FCSTD DOCUMENT  (FreeCAD 0.21R33771 (Git))
Label: jrobot-electronics-print-orientations
License: All rights reserved
LicenseURL: http://en.wikipedia.org/wiki/All_rights_reserved
objects: App::DocumentObjectGroup×3, PartDesign::CoordinateSystem×3, App::Link×2, App::FeaturePython×1, App::Part×1
note: 3 computed .brp shape members not serialized (recipe doc carries the construction recipe); baked Part::Feature solids carry a one-line shape summary decoded from their .brp
EXTERNAL_REF file=jrobot-electronics-parts.FCStd obj=LCS_Origin006
EXTERNAL_REF file=jrobot-electronics-parts.FCStd obj=P_ElectronicsBox
EXTERNAL_REF file=jrobot-electronics-parts.FCStd obj=LCS_Origin007
EXTERNAL_REF file=jrobot-electronics-parts.FCStd obj=P_ElectronicsBox_Cover

FEATURE [App::DocumentObjectGroup] Parts
FEATURE [PartDesign::CoordinateSystem] LCS_Origin
  AttacherType = Attacher::AttachEngine3D
  MapMode = 2
  Support = -> [X_Axis]
FEATURE [App::DocumentObjectGroup] Constraints
FEATURE [App::FeaturePython] Variables  # WARN: FeaturePython — macro-defined, semantics opaque (R4)
  Type = App::PropertyContainer
FEATURE [App::DocumentObjectGroup] Configurations
FEATURE [PartDesign::CoordinateSystem] LCS_ElectronicsBox_Base
  AttacherType = Attacher::AttachEngine3D
FEATURE [PartDesign::CoordinateSystem] LCS_ElectronicsBox_Cover
  AttacherType = Attacher::AttachEngine3D
  Placement = pos=(200,0,0) rot=(0,0,1;0rad)
FEATURE [App::Link] P_ElectronicsBox_Base
  AttachedBy = #LCS_Origin006
  AttachedTo = Parent Assembly#LCS_ElectronicsBox_Base
  LinkedObject = -> <external jrobot-electronics-parts.FCStd>#P_ElectronicsBox
  SolverId = Asm4EE
  expr: Placement = LCS_ElectronicsBox_Base.Placement * AttachmentOffset * jrobot_electronics_parts#LCS_Origin006.Placement ^ -1
FEATURE [App::Link] P_ElectronicsBox_Cover
  AttachedBy = #LCS_Origin007
  AttachedTo = Parent Assembly#LCS_ElectronicsBox_Cover
  AttachmentOffset = pos=(0,0,0) rot=(1,0,0;3.14159rad)
  LinkPlacement = pos=(200,0,0) rot=(1,0,0;3.14159rad)
  LinkedObject = -> <external jrobot-electronics-parts.FCStd>#P_ElectronicsBox_Cover
  Placement = pos=(200,0,0) rot=(1,0,0;3.14159rad)
  SolverId = Asm4EE
  expr: Placement = LCS_ElectronicsBox_Cover.Placement * AttachmentOffset * jrobot_electronics_parts#LCS_Origin007.Placement ^ -1
FEATURE [App::Part] Assembly
  AssemblyType = Part::Link
  Group = -> [LCS_Origin,Constraints,Variables,Configurations,LCS_ElectronicsBox_Base,LCS_ElectronicsBox_Cover,P_ElectronicsBox_Base,P_ElectronicsBox_Cover]
  Origin = -> Origin
  Type = Assembly

RESOLVED EXTERNAL PARTS (link-assembly join: the EXTERNAL_REF files above that resolve inside this repo's crawl, each included once):
---- part jrobot-electronics-parts.FCStd = doc fcstd_2911611a7a01 ----
FCSTD DOCUMENT  (FreeCAD 0.21R33771 (Git))
Label: jrobot-electronics-parts
License: All rights reserved
LicenseURL: http://en.wikipedia.org/wiki/All_rights_reserved
objects: PartDesign::CoordinateSystem×24, Sketcher::SketchObject×16, PartDesign::Pocket×7, PartDesign::Pad×5, PartDesign::Mirrored×3, App::DocumentObjectGroup×3, PartDesign::MultiTransform×2, PartDesign::Body×2, App::Part×2, PartDesign::LinearPattern×2, PartDesign::AdditiveLoft×1
note: 75 computed .brp shape members not serialized (recipe doc carries the construction recipe); baked Part::Feature solids carry a one-line shape summary decoded from their .brp

FEATURE [PartDesign::CoordinateSystem] LCS_ElectronicsBox_Lid
  AttacherType = Attacher::AttachEngine3D
  Placement = pos=(0,0,56) rot=(0,0,1;0rad)
FEATURE [PartDesign::CoordinateSystem] LCS_Origin006  label="LCS_ElectronicsBox_Origin"
  AttacherType = Attacher::AttachEngine3D
  MapMode = 2
  Support = -> [X_Axis026]
FEATURE [Sketcher::SketchObject] Sketch034  label="S_ElectronicsBox_HoleLocations"
  FullyConstrained = true
  Support = -> [XY_Plane027]
  sketch-geometry (27):
    g0: LineSegment StartX=-85 StartY=73 StartZ=0 EndX=-85 EndY=-73 EndZ=0
    g1: LineSegment StartX=-85 StartY=-73 StartZ=0 EndX=85 EndY=-73 EndZ=0
    g2: LineSegment StartX=85 StartY=-73 StartZ=0 EndX=85 EndY=73 EndZ=0
    g3: LineSegment StartX=85 StartY=73 StartZ=0 EndX=-85 EndY=73 EndZ=0
    g4: GeomPoint X=0 Y=0 Z=0
    g5: LineSegment StartX=5 StartY=63 StartZ=0 EndX=74 EndY=63 EndZ=0
    g6: LineSegment StartX=74 StartY=63 StartZ=0 EndX=74 EndY=10 EndZ=0
    g7: LineSegment StartX=74 StartY=10 StartZ=0 EndX=5 EndY=10 EndZ=0
    g8: LineSegment StartX=5 StartY=10 StartZ=0 EndX=5 EndY=63 EndZ=0
    g9: LineSegment StartX=5 StartY=-10 StartZ=0 EndX=74 EndY=-10 EndZ=0
    g10: LineSegment StartX=74 StartY=-10 StartZ=0 EndX=74 EndY=-63 EndZ=0
    g11: LineSegment StartX=74 StartY=-63 StartZ=0 EndX=5 EndY=-63 EndZ=0
    g12: LineSegment StartX=5 StartY=-63 StartZ=0 EndX=5 EndY=-10 EndZ=0
    g13: LineSegment StartX=-60 StartY=54 StartZ=0 EndX=-5 EndY=54 EndZ=0
    g14: LineSegment StartX=-5 StartY=54 StartZ=0 EndX=-5 EndY=-54 EndZ=0
    g15: LineSegment StartX=-5 StartY=-54 StartZ=0 EndX=-60 EndY=-54 EndZ=0
    g16: LineSegment StartX=-60 StartY=-54 StartZ=0 EndX=-60 EndY=54 EndZ=0
    g17: GeomPoint X=19.25 Y=60 Z=0
    g18: GeomPoint X=19.25 Y=13 Z=0
    g19: GeomPoint X=19.25 Y=-60 Z=0
    g20: GeomPoint X=19.25 Y=-13 Z=0
    g21: GeomPoint X=59 Y=37 Z=0
    g22: GeomPoint X=59 Y=-36 Z=0
    g23: GeomPoint X=-56 Y=36.5 Z=0
    g24: GeomPoint X=-8 Y=41.5 Z=0
    g25: GeomPoint X=-56 Y=-39 Z=0
    g26: GeomPoint X=-8 Y=-40.5 Z=0
  constraints (70):
    c: Coincident(g0,g1)
    c: Coincident(g1,g2)
    c: Coincident(g2,g3)
    c: Coincident(g3,g0)
    c: Horizontal(g1)
    c: Horizontal(g3)
    c: Vertical(g0)
    c: Vertical(g2)
    c: Symmetric(g1,g0,g4)
    c: Coincident(g4,g-1)
    c: Coincident(g5,g6)
    c: Coincident(g6,g7)
    c: Coincident(g7,g8)
    c: Coincident(g8,g5)
    c: Horizontal(g5)
    c: Horizontal(g7)
    c: Vertical(g6)
    c: Vertical(g8)
    c: DistanceX(g5,g5) = 69
    c: DistanceY(g6,g6) = 53
    c: Coincident(g9,g10)
    c: Coincident(g10,g11)
    c: Coincident(g11,g12)
    c: Coincident(g12,g9)
    c: Horizontal(g9)
    c: Horizontal(g11)
    c: Vertical(g10)
    c: Vertical(g12)
    c: Equal(g7,g9)
    c: Equal(g6,g10)
    c: Vertical(g7,g9)
    c: DistanceY(g9,g7) = 20
    c: DistanceY(g4,g7) = 10
    c: Coincident(g13,g14)
    c: Coincident(g14,g15)
    c: Coincident(g15,g16)
    c: Coincident(g16,g13)
    c: Horizontal(g13)
    c: Horizontal(g15)
    c: Vertical(g16)
    c: DistanceX(g13,g13) = 55
    c: DistanceY(g14,g14) = 108
    c: DistanceX(g13,g4) = 5
    c: DistanceX(g4,g5) = 5
    c: Symmetric(g13,g14,g-1)
    c: DistanceX(g0,g13) = 25
    c: DistanceY(g17,g5) = 3
    c: DistanceY(g7,g18) = 3
    c: DistanceX(g7,g18) = 14.25
    c: Vertical(g18,g17)
    c: DistanceX(g11,g19) = 14.25
    c: DistanceY(g11,g19) = 3
    c: DistanceY(g20,g9) = 3
    c: Vertical(g20,g19)
    c: Vertical(g21,g22)
    c: DistanceY(g21,g5) = 26
    c: DistanceY(g22,g9) = 26
    c: DistanceY(g2,g2) = 146
    c: DistanceY(g25,g23) = 75.5
    c: DistanceX(g15,g25) = 4
    c: DistanceY(g15,g25) = 15
    c: Vertical(g23,g25)
    c: DistanceY(g14,g26) = 13.5
    c: DistanceX(g26,g14) = 3
    c: Vertical(g24,g26)
    c: DistanceY(g26,g24) = 82
    c: DistanceX(g22,g10) = 15
    c: DistanceY(g18,g17) = 47  'HoleYSeparation1'
    c: DistanceY(g18,g21) = 24  'HoleYSeparation0'
    c: DistanceX(g18,g21) = 39.75  'HoleXSeparation'
FEATURE [Sketcher::SketchObject] Sketch033  label="S_ElectronicsBox_Base"
  ExternalGeometry = -> [Sketch034]
  FullyConstrained = true
  MapMode = 5
  Support = -> [XY_Plane027]
  sketch-geometry (24):
    g0: LineSegment StartX=-85 StartY=73 StartZ=0 EndX=-85 EndY=63 EndZ=0
    g1: LineSegment StartX=-85 StartY=-73 StartZ=0 EndX=85 EndY=-73 EndZ=0
    g2: LineSegment StartX=85 StartY=73 StartZ=0 EndX=-85 EndY=73 EndZ=0
    g3: LineSegment StartX=-85 StartY=63 StartZ=0 EndX=-95 EndY=63 EndZ=0
    g4: LineSegment StartX=-95 StartY=63 StartZ=0 EndX=-95 EndY=53 EndZ=0
    g5: LineSegment StartX=-95 StartY=53 StartZ=0 EndX=-85 EndY=53 EndZ=0
    g6: LineSegment StartX=-85 StartY=-53 StartZ=0 EndX=-95 EndY=-53 EndZ=0
    g7: LineSegment StartX=-95 StartY=-53 StartZ=0 EndX=-95 EndY=-63 EndZ=0
    g8: LineSegment StartX=-95 StartY=-63 StartZ=0 EndX=-85 EndY=-63 EndZ=0
    g9: LineSegment StartX=85 StartY=63 StartZ=0 EndX=95 EndY=63 EndZ=0
    g10: LineSegment StartX=95 StartY=63 StartZ=0 EndX=95 EndY=53 EndZ=0
    g11: LineSegment StartX=95 StartY=53 StartZ=0 EndX=85 EndY=53 EndZ=0
    g12: LineSegment StartX=85 StartY=-53 StartZ=0 EndX=95 EndY=-53 EndZ=0
    g13: LineSegment StartX=95 StartY=-53 StartZ=0 EndX=95 EndY=-63 EndZ=0
    g14: LineSegment StartX=95 StartY=-63 StartZ=0 EndX=85 EndY=-63 EndZ=0
    g15: LineSegment StartX=-85 StartY=-63 StartZ=0 EndX=-85 EndY=-73 EndZ=0
    g16: LineSegment StartX=-85 StartY=53 StartZ=0 EndX=-85 EndY=-53 EndZ=0
    g17: LineSegment StartX=85 StartY=-73 StartZ=0 EndX=85 EndY=-63 EndZ=0
    g18: LineSegment StartX=85 StartY=-53 StartZ=0 EndX=85 EndY=53 EndZ=0
    g19: LineSegment StartX=85 StartY=63 StartZ=0 EndX=85 EndY=73 EndZ=0
    g20: Circle CenterX=-90 CenterY=-58 CenterZ=0 NormalX=0 NormalY=0 NormalZ=1 AngleXU=0 Radius=2.5
    g21: Circle CenterX=-90 CenterY=58 CenterZ=0 NormalX=0 NormalY=0 NormalZ=1 AngleXU=0 Radius=2.5
    g22: Circle CenterX=90 CenterY=58 CenterZ=0 NormalX=0 NormalY=0 NormalZ=1 AngleXU=0 Radius=2.5
    g23: Circle CenterX=90 CenterY=-58 CenterZ=0 NormalX=0 NormalY=0 NormalZ=1 AngleXU=0 Radius=2.5
  constraints (70):
    c: Coincident(g2,g0)
    c: Horizontal(g1)
    c: Horizontal(g2)
    c: Vertical(g0)
    c: Symmetric(g1,g0,g-1)
    c: Coincident(g0,g-3)
    c: Coincident(g3,g4)
    c: Coincident(g4,g5)
    c: Horizontal(g3)
    c: Horizontal(g5)
    c: Vertical(g4)
    c: Coincident(g6,g7)
    c: Coincident(g7,g8)
    c: Horizontal(g6)
    c: Horizontal(g8)
    c: Vertical(g7)
    c: PointOnObject(g6,g0)
    c: Coincident(g9,g10)
    c: Coincident(g10,g11)
    c: Horizontal(g9)
    c: Horizontal(g11)
    c: Vertical(g10)
    c: Coincident(g12,g13)
    c: Coincident(g13,g14)
    c: Horizontal(g12)
    c: Horizontal(g14)
    c: Vertical(g13)
    c: Horizontal(g3,g9)
    c: Horizontal(g5,g11)
    c: Horizontal(g12,g6)
    c: Horizontal(g8,g14)
    c: DistanceY(g7,g7) = 10
    c: Equal(g7,g4)
    c: DistanceX(g8,g8) = 10
    c: Equal(g8,g14)
    c: Vertical(g10,g12)
    c: Equal(g5,g8)
    c: DistanceY(g1,g8) = 10
    c: DistanceY(g3,g0) = 10
    c: Coincident(g0,g3)
    c: Vertical(g5,g0)
    c: Coincident(g15,g8)
    c: Coincident(g15,g1)
    c: Vertical(g15)
    c: Vertical(g6,g1)
    c: Coincident(g16,g5)
    c: Coincident(g16,g6)
    c: Coincident(g17,g1)
    c: Coincident(g17,g14)
    c: Vertical(g17)
    c: Coincident(g18,g12)
    c: Coincident(g18,g11)
    c: Vertical(g18)
    c: Coincident(g19,g9)
    c: Coincident(g19,g2)
    c: Vertical(g19)
    c: Vertical(g18,g9)
    c: DistanceX(g0,g2) = 170
    c: Diameter(g20) = 5
    c: DistanceX(g20,g6) = 5
    c: DistanceY(g8,g20) = 5
    c: DistanceY(g21,g0) = 5
    c: DistanceX(g21,g0) = 5
    c: Diameter(g21) = 5
    c: Diameter(g23) = 5
    c: Diameter(g22) = 5
    c: DistanceX(g9,g22) = 5
    c: Horizontal(g21,g22)
    c: Horizontal(g20,g23)
    c: Vertical(g23,g22)
FEATURE [PartDesign::Pad] Pad016  label="PAD_ElectronicsBox_Base"
  Direction = (0,0,1)
  Length = 2
  Length2 = 10
  Profile = -> Sketch033
  ReferenceAxis = -> Sketch033 [N_Axis]
  Type = 0
FEATURE [Sketcher::SketchObject] Sketch035  label="S_ElectronicsBox_HolePads"
  ExternalGeometry = -> [Sketch034]
  FullyConstrained = true
  MapMode = 5
  Placement = pos=(0,0,1.5) rot=(0,0,1;0rad)
  sketch-geometry (50):
    g0: LineSegment StartX=-61 StartY=41.5 StartZ=0 EndX=-61 EndY=31.5 EndZ=0
    g1: LineSegment StartX=-61 StartY=31.5 StartZ=0 EndX=-51 EndY=31.5 EndZ=0
    g2: LineSegment StartX=-51 StartY=31.5 StartZ=0 EndX=-51 EndY=41.5 EndZ=0
    g3: LineSegment StartX=-51 StartY=41.5 StartZ=0 EndX=-61 EndY=41.5 EndZ=0
    g4: GeomPoint X=-56 Y=36.5 Z=0
    g5: LineSegment StartX=-61 StartY=-34 StartZ=0 EndX=-61 EndY=-44 EndZ=0
    g6: LineSegment StartX=-61 StartY=-44 StartZ=0 EndX=-51 EndY=-44 EndZ=0
    g7: LineSegment StartX=-51 StartY=-44 StartZ=0 EndX=-51 EndY=-34 EndZ=0
    g8: LineSegment StartX=-51 StartY=-34 StartZ=0 EndX=-61 EndY=-34 EndZ=0
    g9: GeomPoint X=-56 Y=-39 Z=0
    g10: LineSegment StartX=-13 StartY=46.5 StartZ=0 EndX=-13 EndY=36.5 EndZ=0
    g11: LineSegment StartX=-13 StartY=36.5 StartZ=0 EndX=-3 EndY=36.5 EndZ=0
    g12: LineSegment StartX=-3 StartY=36.5 StartZ=0 EndX=-3 EndY=46.5 EndZ=0
    g13: LineSegment StartX=-3 StartY=46.5 StartZ=0 EndX=-13 EndY=46.5 EndZ=0
    g14: GeomPoint X=-8 Y=41.5 Z=0
    g15: LineSegment StartX=-13 StartY=-35.5 StartZ=0 EndX=-13 EndY=-45.5 EndZ=0
    g16: LineSegment StartX=-13 StartY=-45.5 StartZ=0 EndX=-3 EndY=-45.5 EndZ=0
    g17: LineSegment StartX=-3 StartY=-45.5 StartZ=0 EndX=-3 EndY=-35.5 EndZ=0
    g18: LineSegment StartX=-3 StartY=-35.5 StartZ=0 EndX=-13 EndY=-35.5 EndZ=0
    g19: GeomPoint X=-8 Y=-40.5 Z=0
    g20: LineSegment StartX=14.25 StartY=65 StartZ=0 EndX=14.25 EndY=55 EndZ=0
    g21: LineSegment StartX=14.25 StartY=55 StartZ=0 EndX=24.25 EndY=55 EndZ=0
    g22: LineSegment StartX=24.25 StartY=55 StartZ=0 EndX=24.25 EndY=65 EndZ=0
    g23: LineSegment StartX=24.25 StartY=65 StartZ=0 EndX=14.25 EndY=65 EndZ=0
    g24: GeomPoint X=19.25 Y=60 Z=0
    g25: LineSegment StartX=54 StartY=42 StartZ=0 EndX=54 EndY=32 EndZ=0
    g26: LineSegment StartX=54 StartY=32 StartZ=0 EndX=64 EndY=32 EndZ=0
    g27: LineSegment StartX=64 StartY=32 StartZ=0 EndX=64 EndY=42 EndZ=0
    g28: LineSegment StartX=64 StartY=42 StartZ=0 EndX=54 EndY=42 EndZ=0
    g29: GeomPoint X=59 Y=37 Z=0
    g30: LineSegment StartX=14.25 StartY=18 StartZ=0 EndX=14.25 EndY=8 EndZ=0
    g31: LineSegment StartX=14.25 StartY=8 StartZ=0 EndX=24.25 EndY=8 EndZ=0
    g32: LineSegment StartX=24.25 StartY=8 StartZ=0 EndX=24.25 EndY=18 EndZ=0
    g33: LineSegment StartX=24.25 StartY=18 StartZ=0 EndX=14.25 EndY=18 EndZ=0
    g34: GeomPoint X=19.25 Y=13 Z=0
    g35: LineSegment StartX=14.25 StartY=-8 StartZ=0 EndX=14.25 EndY=-18 EndZ=0
    g36: LineSegment StartX=14.25 StartY=-18 StartZ=0 EndX=24.25 EndY=-18 EndZ=0
    g37: LineSegment StartX=24.25 StartY=-18 StartZ=0 EndX=24.25 EndY=-8 EndZ=0
    g38: LineSegment StartX=24.25 StartY=-8 StartZ=0 EndX=14.25 EndY=-8 EndZ=0
    g39: GeomPoint X=19.25 Y=-13 Z=0
    g40: LineSegment StartX=54 StartY=-31 StartZ=0 EndX=54 EndY=-41 EndZ=0
    g41: LineSegment StartX=54 StartY=-41 StartZ=0 EndX=64 EndY=-41 EndZ=0
    g42: LineSegment StartX=64 StartY=-41 StartZ=0 EndX=64 EndY=-31 EndZ=0
    g43: LineSegment StartX=64 StartY=-31 StartZ=0 EndX=54 EndY=-31 EndZ=0
    g44: GeomPoint X=59 Y=-36 Z=0
    g45: LineSegment StartX=14.25 StartY=-55 StartZ=0 EndX=14.25 EndY=-65 EndZ=0
    g46: LineSegment StartX=14.25 StartY=-65 StartZ=0 EndX=24.25 EndY=-65 EndZ=0
    g47: LineSegment StartX=24.25 StartY=-65 StartZ=0 EndX=24.25 EndY=-55 EndZ=0
    g48: LineSegment StartX=24.25 StartY=-55 StartZ=0 EndX=14.25 EndY=-55 EndZ=0
    g49: GeomPoint X=19.25 Y=-60 Z=0
  constraints (120):
    c: Coincident(g0,g1)
    c: Coincident(g1,g2)
    c: Coincident(g2,g3)
    c: Coincident(g3,g0)
    c: Horizontal(g1)
    c: Horizontal(g3)
    c: Vertical(g0)
    c: Vertical(g2)
    c: Symmetric(g1,g0,g4)
    c: Coincident(g5,g6)
    c: Coincident(g6,g7)
    c: Coincident(g7,g8)
    c: Coincident(g8,g5)
    c: Horizontal(g6)
    c: Horizontal(g8)
    c: Vertical(g5)
    c: Vertical(g7)
    c: Symmetric(g6,g5,g9)
    c: Coincident(g10,g11)
    c: Coincident(g11,g12)
    c: Coincident(g12,g13)
    c: Coincident(g13,g10)
    c: Horizontal(g11)
    c: Horizontal(g13)
    c: Vertical(g10)
    c: Vertical(g12)
    c: Symmetric(g11,g10,g14)
    c: Coincident(g15,g16)
    c: Coincident(g16,g17)
    c: Coincident(g17,g18)
    c: Coincident(g18,g15)
    c: Horizontal(g16)
    c: Horizontal(g18)
    c: Vertical(g15)
    c: Vertical(g17)
    c: Symmetric(g16,g15,g19)
    c: Coincident(g20,g21)
    c: Coincident(g21,g22)
    c: Coincident(g22,g23)
    c: Coincident(g23,g20)
    c: Horizontal(g21)
    c: Horizontal(g23)
    c: Vertical(g20)
    c: Vertical(g22)
    c: Symmetric(g21,g20,g24)
    c: Coincident(g25,g26)
    c: Coincident(g26,g27)
    c: Coincident(g27,g28)
    c: Coincident(g28,g25)
    c: Horizontal(g26)
    c: Horizontal(g28)
    c: Vertical(g25)
    c: Vertical(g27)
    c: Symmetric(g26,g25,g29)
    c: Coincident(g30,g31)
    c: Coincident(g31,g32)
    c: Coincident(g32,g33)
    c: Coincident(g33,g30)
    c: Horizontal(g31)
    c: Horizontal(g33)
    c: Vertical(g30)
    c: Vertical(g32)
    c: Symmetric(g31,g30,g34)
    c: Coincident(g35,g36)
    c: Coincident(g36,g37)
    c: Coincident(g37,g38)
    c: Coincident(g38,g35)
    c: Horizontal(g36)
    c: Horizontal(g38)
    c: Vertical(g35)
    c: Vertical(g37)
    c: Symmetric(g36,g35,g39)
    c: Coincident(g40,g41)
    c: Coincident(g41,g42)
    c: Coincident(g42,g43)
    c: Coincident(g43,g40)
    c: Horizontal(g41)
    c: Horizontal(g43)
    c: Vertical(g40)
    c: Vertical(g42)
    c: Symmetric(g41,g40,g44)
    c: Coincident(g45,g46)
    c: Coincident(g46,g47)
    c: Coincident(g47,g48)
    c: Coincident(g48,g45)
    c: Horizontal(g46)
    c: Horizontal(g48)
    c: Vertical(g45)
    c: Vertical(g47)
    c: Symmetric(g46,g45,g49)
    c: Coincident(g4,g-3)
    c: Coincident(g9,g-12)
    c: Coincident(g19,g-9)
    c: Coincident(g14,g-4)
    c: Coincident(g24,g-11)
    c: Coincident(g29,g-6)
    c: Coincident(g34,g-5)
    c: Coincident(g39,g-10)
    c: Coincident(g44,g-7)
    c: Coincident(g49,g-8)
    c: Equal(g3,g2)
    c: Equal(g8,g7)
    c: Equal(g18,g17)
    c: Equal(g13,g12)
    c: Equal(g33,g32)
    c: Equal(g38,g37)
    c: Equal(g48,g47)
    c: Equal(g43,g42)
    c: Equal(g28,g27)
    c: Equal(g23,g22)
    c: Equal(g3,g8)
    c: Equal(g3,g13)
    c: Equal(g13,g23)
    c: Equal(g23,g28)
    c: Equal(g28,g33)
    c: Equal(g33,g38)
    c: Equal(g38,g48)
    c: Equal(g18,g8)
    c: Equal(g48,g43)
    c: DistanceX(g3,g3) = 10
FEATURE [Sketcher::SketchObject] Sketch036  label="S_ElectronicsBox_Holes"
  AttachmentOffset = pos=(2,0,0) rot=(0,0,1;0rad)
  ExternalGeometry = -> [Sketch034]
  FullyConstrained = true
  MapMode = 5
  Placement = pos=(2,0,0) rot=(1,0,0;3.14159rad)
  sketch-geometry (10):
    g0: Circle CenterX=-58 CenterY=39 CenterZ=0 NormalX=0 NormalY=0 NormalZ=1 AngleXU=0 Radius=1.75
    g1: Circle CenterX=-10 CenterY=40.5 CenterZ=0 NormalX=0 NormalY=0 NormalZ=1 AngleXU=0 Radius=1.75
    g2: Circle CenterX=-10 CenterY=-41.5 CenterZ=0 NormalX=0 NormalY=0 NormalZ=1 AngleXU=0 Radius=1.75
    g3: Circle CenterX=-58 CenterY=-36.5 CenterZ=0 NormalX=0 NormalY=0 NormalZ=1 AngleXU=0 Radius=1.75
    g4: Circle CenterX=17.25 CenterY=13 CenterZ=0 NormalX=0 NormalY=0 NormalZ=1 AngleXU=0 Radius=1.75
    g5: Circle CenterX=17.25 CenterY=60 CenterZ=0 NormalX=0 NormalY=0 NormalZ=1 AngleXU=0 Radius=1.75
    g6: Circle CenterX=57 CenterY=36 CenterZ=0 NormalX=0 NormalY=0 NormalZ=1 AngleXU=0 Radius=1.75
    g7: Circle CenterX=57 CenterY=-37 CenterZ=0 NormalX=0 NormalY=0 NormalZ=1 AngleXU=0 Radius=1.75
    g8: Circle CenterX=17.25 CenterY=-13 CenterZ=0 NormalX=0 NormalY=0 NormalZ=1 AngleXU=0 Radius=1.75
    g9: Circle CenterX=17.25 CenterY=-60 CenterZ=0 NormalX=0 NormalY=0 NormalZ=1 AngleXU=0 Radius=1.75
  constraints (20):
    c: Coincident(g0,g-3)
    c: Coincident(g1,g-4)
    c: Coincident(g2,g-5)
    c: Coincident(g3,g-6)
    c: Coincident(g4,g-12)
    c: Coincident(g5,g-11)
    c: Coincident(g6,g-10)
    c: Coincident(g7,g-9)
    c: Coincident(g8,g-8)
    c: Coincident(g9,g-7)
    c: Equal(g0,g1)
    c: Equal(g1,g2)
    c: Equal(g2,g3)
    c: Equal(g3,g8)
    c: Equal(g8,g9)
    c: Equal(g9,g7)
    c: Equal(g7,g4)
    c: Equal(g4,g6)
    c: Equal(g6,g5)
    c: Diameter(g0) = 3.5
FEATURE [Sketcher::SketchObject] Sketch037  label="S_ElectronicsBox_BoltIndent"
  ExternalGeometry = -> [Sketch034]
  FullyConstrained = true
  MapMode = 5
  Placement = pos=(0,0,0) rot=(1,0,0;3.14159rad)
  sketch-geometry (10):
    g0: Circle CenterX=-56 CenterY=39 CenterZ=0 NormalX=0 NormalY=0 NormalZ=1 AngleXU=0 Radius=3
    g1: Circle CenterX=-8 CenterY=40.5 CenterZ=0 NormalX=0 NormalY=0 NormalZ=1 AngleXU=0 Radius=3
    g2: Circle CenterX=-8 CenterY=-41.5 CenterZ=0 NormalX=0 NormalY=0 NormalZ=1 AngleXU=0 Radius=3
    g3: Circle CenterX=-56 CenterY=-36.5 CenterZ=0 NormalX=0 NormalY=0 NormalZ=1 AngleXU=0 Radius=3
    g4: Circle CenterX=19.25 CenterY=13 CenterZ=0 NormalX=0 NormalY=0 NormalZ=1 AngleXU=0 Radius=3
    g5: Circle CenterX=19.25 CenterY=60 CenterZ=0 NormalX=0 NormalY=0 NormalZ=1 AngleXU=0 Radius=3
    g6: Circle CenterX=59 CenterY=36 CenterZ=0 NormalX=0 NormalY=0 NormalZ=1 AngleXU=0 Radius=3
    g7: Circle CenterX=59 CenterY=-37 CenterZ=0 NormalX=0 NormalY=0 NormalZ=1 AngleXU=0 Radius=3
    g8: Circle CenterX=19.25 CenterY=-13 CenterZ=0 NormalX=0 NormalY=0 NormalZ=1 AngleXU=0 Radius=3
    g9: Circle CenterX=19.25 CenterY=-60 CenterZ=0 NormalX=0 NormalY=0 NormalZ=1 AngleXU=0 Radius=3
  constraints (20):
    c: Coincident(g0,g-3)
    c: Coincident(g1,g-4)
    c: Coincident(g2,g-5)
    c: Coincident(g3,g-6)
    c: Coincident(g4,g-12)
    c: Coincident(g5,g-11)
    c: Coincident(g6,g-10)
    c: Coincident(g7,g-9)
    c: Coincident(g8,g-8)
    c: Coincident(g9,g-7)
    c: Equal(g0,g1)
    c: Equal(g1,g2)
    c: Equal(g2,g3)
    c: Equal(g3,g8)
    c: Equal(g8,g9)
    c: Equal(g9,g7)
    c: Equal(g7,g4)
    c: Equal(g4,g6)
    c: Equal(g6,g5)
    c: Diameter(g0) = 6
FEATURE [Sketcher::SketchObject] Sketch038  label="S_ElectronicsBox_Switches"
  FullyConstrained = true
  MapMode = 5
  Placement = pos=(0,-73,0) rot=(1,0,0;1.5708rad)
  sketch-geometry (10):
    g0: LineSegment StartX=1.16 StartY=46 StartZ=0 EndX=13.66 EndY=46 EndZ=0
    g1: LineSegment StartX=13.66 StartY=46 StartZ=0 EndX=13.66 EndY=25 EndZ=0
    g2: LineSegment StartX=13.66 StartY=25 StartZ=0 EndX=1.16 EndY=25 EndZ=0
    g3: LineSegment StartX=1.16 StartY=25 StartZ=0 EndX=1.16 EndY=46 EndZ=0
    g4: LineSegment StartX=-54 StartY=31 StartZ=0 EndX=-34 EndY=31 EndZ=0
    g5: LineSegment StartX=-34 StartY=31 StartZ=0 EndX=-34 EndY=16 EndZ=0
    g6: LineSegment StartX=-34 StartY=16 StartZ=0 EndX=-54 EndY=16 EndZ=0
    g7: LineSegment StartX=-54 StartY=16 StartZ=0 EndX=-54 EndY=31 EndZ=0
    g8: GeomPoint X=-44 Y=23.5 Z=0
    g9: GeomPoint X=7.41 Y=35.5 Z=0
  constraints (30):
    c: Coincident(g0,g1)
    c: Coincident(g1,g2)
    c: Coincident(g2,g3)
    c: Coincident(g3,g0)
    c: Horizontal(g0)
    c: Horizontal(g2)
    c: Vertical(g1)
    c: Vertical(g3)
    c: DistanceX(g0,g0) = 12.5
    c: DistanceY(g3,g3) = 21
    c: Coincident(g4,g5)
    c: Coincident(g5,g6)
    c: Coincident(g6,g7)
    c: Coincident(g7,g4)
    c: Horizontal(g4)
    c: Horizontal(g6)
    c: Vertical(g5)
    c: Vertical(g7)
    c: DistanceY(g-1,g5) = 16
    c: DistanceY(g6,g4) = 15
    c: DistanceX(g4,g4) = 20
    c: DistanceX(g5,g-1) = 34
    c: DistanceX(g-1,g2) = 1.16
    c: DistanceY(g-1,g1) = 25
    c: Symmetric(g1,g0,g9)
    c: Symmetric(g4,g5,g8)
    c: DistanceY(g-1,g8) = 23.5  'USBY'
    c: DistanceX(g8,g-1) = 44  'USBX'
    c: DistanceY(g-1,g9) = 35.5  'SwitchY'
    c: DistanceX(g-1,g9) = 7.41  'SwitchX'
FEATURE [Sketcher::SketchObject] Sketch039  label="S_ElectronicsBox_WallsBase"
  ExternalGeometry = -> [Sketch034,Sketch033]
  FullyConstrained = true
  MapMode = 2
  Support = -> [Pad016]
  sketch-geometry (8):
    g0: LineSegment StartX=-85 StartY=73 StartZ=0 EndX=85 EndY=73 EndZ=0
    g1: LineSegment StartX=85 StartY=73 StartZ=0 EndX=85 EndY=70 EndZ=0
    g2: LineSegment StartX=85 StartY=70 StartZ=0 EndX=-85 EndY=70 EndZ=0
    g3: LineSegment StartX=-85 StartY=70 StartZ=0 EndX=-85 EndY=73 EndZ=0
    g4: LineSegment StartX=-85 StartY=-73 StartZ=0 EndX=85 EndY=-73 EndZ=0
    g5: LineSegment StartX=85 StartY=-73 StartZ=0 EndX=85 EndY=-70 EndZ=0
    g6: LineSegment StartX=85 StartY=-70 StartZ=0 EndX=-85 EndY=-70 EndZ=0
    g7: LineSegment StartX=-85 StartY=-70 StartZ=0 EndX=-85 EndY=-73 EndZ=0
  constraints (20):
    c: Coincident(g0,g1)
    c: Coincident(g1,g2)
    c: Coincident(g2,g3)
    c: Coincident(g3,g0)
    c: Horizontal(g2)
    c: Vertical(g1)
    c: Vertical(g3)
    c: Coincident(g0,g-3)
    c: Coincident(g0,g-4)
    c: DistanceY(g3,g3) = 3
    c: Coincident(g4,g5)
    c: Coincident(g5,g6)
    c: Coincident(g6,g7)
    c: Coincident(g7,g4)
    c: Horizontal(g6)
    c: Vertical(g5)
    c: Vertical(g7)
    c: Coincident(g4,g-6)
    c: Coincident(g4,g-5)
    c: DistanceY(g7,g7) = 3
FEATURE [PartDesign::Pad] Pad017  label="PAD_ElectronicsBoxWalls"
  BaseFeature = -> Pad016
  Direction = (0,0,1)
  Length = 56
  Length2 = 10
  Profile = -> Sketch039
  ReferenceAxis = -> Sketch039 [N_Axis]
  Type = 0
FEATURE [Sketcher::SketchObject] Sketch041  label="S_ElectronicsBox_TopTabBase"
  FullyConstrained = false
  MapMode = 2
  Placement = pos=(0,0,46) rot=(0,0,1;0rad)
  sketch-geometry (4):
    g0: LineSegment StartX=-79 StartY=72.75 StartZ=0 EndX=-69 EndY=72.75 EndZ=0
    g1: LineSegment StartX=-69 StartY=72.75 StartZ=0 EndX=-69 EndY=73 EndZ=0
    g2: LineSegment StartX=-69 StartY=73 StartZ=0 EndX=-79 EndY=73 EndZ=0
    g3: LineSegment StartX=-79 StartY=73 StartZ=0 EndX=-79 EndY=72.75 EndZ=0
  constraints (9):
    c: Coincident(g0,g1)
    c: Coincident(g1,g2)
    c: Coincident(g2,g3)
    c: Coincident(g3,g0)
    c: Horizontal(g0)
    c: Horizontal(g2)
    c: Vertical(g1)
    c: Vertical(g3)
    c: DistanceX(g0,g0) = 10
FEATURE [Sketcher::SketchObject] Sketch042  label="S_ElectronicsBox_TopTabTop"
  ExternalGeometry = -> [Sketch039,Sketch033]
  FullyConstrained = true
  MapMode = 2
  Placement = pos=(0,0,56) rot=(0,0,1;0rad)
  sketch-geometry (4):
    g0: LineSegment StartX=-79 StartY=81 StartZ=0 EndX=-69 EndY=81 EndZ=0
    g1: LineSegment StartX=-69 StartY=81 StartZ=0 EndX=-69 EndY=73 EndZ=0
    g2: LineSegment StartX=-69 StartY=73 StartZ=0 EndX=-79 EndY=73 EndZ=0
    g3: LineSegment StartX=-79 StartY=73 StartZ=0 EndX=-79 EndY=81 EndZ=0
  constraints (12):
    c: Coincident(g0,g1)
    c: Coincident(g1,g2)
    c: Coincident(g2,g3)
    c: Coincident(g3,g0)
    c: Horizontal(g0)
    c: Horizontal(g2)
    c: Vertical(g1)
    c: Vertical(g3)
    c: DistanceX(g0,g0) = 10
    c: DistanceX(g-4,g0) = 6
    c: DistanceY(g-4,g0) = 8
    c: Horizontal(g2,g-4)
FEATURE [Sketcher::SketchObject] Sketch040  label="S_ElectronicsBox_WallsTopHoles"
  ExternalGeometry = -> [Sketch042]
  FullyConstrained = true
  MapMode = 5
  Placement = pos=(0,0,59) rot=(0,0,1;0rad)
  sketch-geometry (5):
    g0: Circle CenterX=-74 CenterY=77 CenterZ=0 NormalX=0 NormalY=0 NormalZ=1 AngleXU=0 Radius=1.5
    g1: LineSegment StartX=-79 StartY=81 StartZ=0 EndX=-79 EndY=77 EndZ=0
    g2: LineSegment StartX=-79 StartY=77 StartZ=0 EndX=-79 EndY=73 EndZ=0
    g3: LineSegment StartX=-79 StartY=81 StartZ=0 EndX=-74 EndY=81 EndZ=0
    g4: LineSegment StartX=-74 StartY=81 StartZ=0 EndX=-69 EndY=81 EndZ=0
  constraints (13):
    c: Diameter(g0) = 3
    c: Coincident(g1,g-3)
    c: Vertical(g1)
    c: Coincident(g2,g1)
    c: Coincident(g2,g-5)
    c: Coincident(g3,g1)
    c: Horizontal(g3)
    c: Coincident(g4,g3)
    c: Coincident(g4,g-4)
    c: Equal(g3,g4)
    c: Equal(g1,g2)
    c: Vertical(g0,g3)
    c: Horizontal(g1,g0)
FEATURE [Sketcher::SketchObject] Sketch043  label="S_ElectronicsBox_TopTabMid"
  AttachmentOffset = pos=(0,0,-6) rot=(0,0,1;0rad)
  ExternalGeometry = -> [Sketch039,Sketch033]
  FullyConstrained = true
  MapMode = 2
  Placement = pos=(0,0,50) rot=(0,0,1;0rad)
  sketch-geometry (4):
    g0: LineSegment StartX=-79 StartY=81 StartZ=0 EndX=-69 EndY=81 EndZ=0
    g1: LineSegment StartX=-69 StartY=81 StartZ=0 EndX=-69 EndY=73 EndZ=0
    g2: LineSegment StartX=-69 StartY=73 StartZ=0 EndX=-79 EndY=73 EndZ=0
    g3: LineSegment StartX=-79 StartY=73 StartZ=0 EndX=-79 EndY=81 EndZ=0
  constraints (12):
    c: Coincident(g3,g0)
    c: Horizontal(g0)
    c: Horizontal(g2)
    c: Vertical(g1)
    c: Vertical(g3)
    c: DistanceX(g0,g0) = 10
    c: DistanceX(g-4,g0) = 6
    c: DistanceY(g-4,g0) = 8
    c: Coincident(g1,g2)
    c: Coincident(g2,g3)
    c: Coincident(g0,g1)
    c: Horizontal(g2,g-4)
FEATURE [PartDesign::AdditiveLoft] AdditiveLoft  label="LOFT_ElectronicsBox_Tabs"
  BaseFeature = -> Pad017
  Closed = false
  Profile = -> Sketch041
  Ruled = false
  Sections = -> [Sketch043,Sketch042]
FEATURE [PartDesign::Pocket] Pocket014  label="POCKET_ElectronicsBox_WallsTopHoles"
  BaseFeature = -> AdditiveLoft
  Direction = (0,0,-1)
  Length = 20
  Length2 = 5
  Profile = -> Sketch040
  ReferenceAxis = -> Sketch040 [N_Axis]
  Type = 0
FEATURE [Sketcher::SketchObject] Sketch045  label="S_ElectronicsBox_BackWires"
  FullyConstrained = false
  MapMode = 5
  Placement = pos=(0,73,0) rot=(0,0.707107,0.707107;3.14159rad)
  sketch-geometry (9):
    g0: LineSegment StartX=-55.46 StartY=40 StartZ=0 EndX=-30.46 EndY=40 EndZ=0
    g1: LineSegment StartX=-30.46 StartY=40 StartZ=0 EndX=-30.46 EndY=30 EndZ=0
    g2: LineSegment StartX=-30.46 StartY=30 StartZ=0 EndX=-55.46 EndY=30 EndZ=0
    g3: LineSegment StartX=-55.46 StartY=30 StartZ=0 EndX=-55.46 EndY=40 EndZ=0
    g4: LineSegment StartX=9.54003 StartY=40 StartZ=0 EndX=34.54 EndY=40 EndZ=0
    g5: LineSegment StartX=34.54 StartY=40 StartZ=0 EndX=34.54 EndY=30 EndZ=0
    g6: LineSegment StartX=34.54 StartY=30 StartZ=0 EndX=9.54003 EndY=30 EndZ=0
    g7: LineSegment StartX=9.54003 StartY=30 StartZ=0 EndX=9.54003 EndY=40 EndZ=0
    g8: Circle CenterX=44 CenterY=20 CenterZ=0 NormalX=0 NormalY=0 NormalZ=1 AngleXU=0 Radius=4
  constraints (26):
    c: Coincident(g0,g1)
    c: Coincident(g1,g2)
    c: Coincident(g2,g3)
    c: Coincident(g3,g0)
    c: Horizontal(g0)
    c: Horizontal(g2)
    c: Vertical(g1)
    c: Vertical(g3)
    c: Coincident(g4,g5)
    c: Coincident(g5,g6)
    c: Coincident(g6,g7)
    c: Coincident(g7,g4)
    c: Horizontal(g4)
    c: Horizontal(g6)
    c: Vertical(g5)
    c: Vertical(g7)
    c: Equal(g1,g7)
    c: Equal(g0,g4)
    c: DistanceY(g-1,g1) = 30
    c: DistanceX(g0,g0) = 25
    c: DistanceY(g1,g1) = 10
    c: DistanceX(g0,g4) = 40
    c: Diameter(g8) = 8
    c: Horizontal(g0,g4)
    c: DistanceY(g-1,g8) = 20  'PowerY'
    c: DistanceX(g-1,g8) = 44  'PowerX'
FEATURE [PartDesign::CoordinateSystem] LCS_Origin007  label="LCS_ElectronicsBox_Cover"
  AttacherType = Attacher::AttachEngine3D
  MapMode = 2
  Support = -> [X_Axis028]
FEATURE [Sketcher::SketchObject] Sketch046  label="S_ElectronicsBox_Cover"
  FullyConstrained = true
  MapMode = 5
  Support = -> [XY_Plane029]
  sketch-geometry (33):
    g0: LineSegment StartX=-85 StartY=-81 StartZ=0 EndX=-85 EndY=81 EndZ=0
    g1: LineSegment StartX=-85 StartY=81 StartZ=0 EndX=85 EndY=81 EndZ=0
    g2: LineSegment StartX=85 StartY=81 StartZ=0 EndX=85 EndY=-81 EndZ=0
    g3: LineSegment StartX=85 StartY=-81 StartZ=0 EndX=-85 EndY=-81 EndZ=0
    g4: GeomPoint X=0 Y=0 Z=0
    g5: Circle CenterX=-74 CenterY=77 CenterZ=0 NormalX=0 NormalY=0 NormalZ=1 AngleXU=0 Radius=1.5
    g6: Circle CenterX=74 CenterY=77 CenterZ=0 NormalX=0 NormalY=0 NormalZ=1 AngleXU=0 Radius=1.5
    g7: Circle CenterX=74 CenterY=-77 CenterZ=0 NormalX=0 NormalY=0 NormalZ=1 AngleXU=0 Radius=1.5
    g8: Circle CenterX=-74 CenterY=-77 CenterZ=0 NormalX=0 NormalY=0 NormalZ=1 AngleXU=0 Radius=1.5
    g9: LineSegment StartX=20.25 StartY=47 StartZ=0 EndX=40 EndY=47 EndZ=0
    g10: LineSegment StartX=40 StartY=47 StartZ=0 EndX=40 EndY=27.25 EndZ=0
    g11: LineSegment StartX=40 StartY=27.25 StartZ=0 EndX=20.25 EndY=27.25 EndZ=0
    g12: LineSegment StartX=20.25 StartY=27.25 StartZ=0 EndX=20.25 EndY=47 EndZ=0
    g13: Circle CenterX=18.25 CenterY=49 CenterZ=0 NormalX=0 NormalY=0 NormalZ=1 AngleXU=0 Radius=1.5
    g14: Circle CenterX=42 CenterY=49 CenterZ=0 NormalX=0 NormalY=0 NormalZ=1 AngleXU=0 Radius=1.5
    g15: Circle CenterX=42 CenterY=25.25 CenterZ=0 NormalX=0 NormalY=0 NormalZ=1 AngleXU=0 Radius=1.5
    g16: Circle CenterX=18.25 CenterY=25.25 CenterZ=0 NormalX=0 NormalY=0 NormalZ=1 AngleXU=0 Radius=1.5
    g17: Circle CenterX=18.25 CenterY=-22.75 CenterZ=0 NormalX=0 NormalY=0 NormalZ=1 AngleXU=0 Radius=1.5
    g18: Circle CenterX=42 CenterY=-22.75 CenterZ=0 NormalX=0 NormalY=0 NormalZ=1 AngleXU=0 Radius=1.5
    g19: Circle CenterX=18.25 CenterY=-46.5 CenterZ=0 NormalX=0 NormalY=0 NormalZ=1 AngleXU=0 Radius=1.5
    g20: Circle CenterX=42 CenterY=-46.5 CenterZ=0 NormalX=0 NormalY=0 NormalZ=1 AngleXU=0 Radius=1.5
    g21: LineSegment StartX=20.25 StartY=-24.75 StartZ=0 EndX=40 EndY=-24.75 EndZ=0
    g22: LineSegment StartX=40 StartY=-24.75 StartZ=0 EndX=40 EndY=-44.5 EndZ=0
    g23: LineSegment StartX=40 StartY=-44.5 StartZ=0 EndX=20.25 EndY=-44.5 EndZ=0
    g24: LineSegment StartX=20.25 StartY=-44.5 StartZ=0 EndX=20.25 EndY=-24.75 EndZ=0
    g25: LineSegment StartX=15.25 StartY=46 StartZ=0 EndX=8.25 EndY=46 EndZ=0
    g26: LineSegment StartX=8.25 StartY=46 StartZ=0 EndX=8.25 EndY=38 EndZ=0
    g27: LineSegment StartX=8.25 StartY=38 StartZ=0 EndX=15.25 EndY=38 EndZ=0
    g28: LineSegment StartX=15.25 StartY=38 StartZ=0 EndX=15.25 EndY=46 EndZ=0
    g29: LineSegment StartX=15.25 StartY=-25.75 StartZ=0 EndX=8.25 EndY=-25.75 EndZ=0
    g30: LineSegment StartX=8.25 StartY=-25.75 StartZ=0 EndX=8.25 EndY=-33.75 EndZ=0
    g31: LineSegment StartX=8.25 StartY=-33.75 StartZ=0 EndX=15.25 EndY=-33.75 EndZ=0
    g32: LineSegment StartX=15.25 StartY=-33.75 StartZ=0 EndX=15.25 EndY=-25.75 EndZ=0
  constraints (96):
    c: Coincident(g0,g1)
    c: Coincident(g1,g2)
    c: Coincident(g2,g3)
    c: Coincident(g3,g0)
    c: Horizontal(g1)
    c: Horizontal(g3)
    c: Vertical(g0)
    c: Vertical(g2)
    c: Symmetric(g1,g0,g4)
    c: Coincident(g4,g-1)
    c: DistanceY(g0,g0) = 162
    c: DistanceX(g1,g1) = 170
    c: Equal(g5,g6)
    c: Equal(g6,g8)
    c: Equal(g8,g7)
    c: Diameter(g5) = 3
    c: Horizontal(g5,g6)
    c: Vertical(g5,g8)
    c: Vertical(g7,g6)
    c: DistanceX(g0,g5) = 11
    c: DistanceY(g5,g0) = 4
    c: Horizontal(g7,g8)
    c: DistanceX(g5,g6) = 148
    c: DistanceY(g0,g8) = 4
    c: Coincident(g9,g10)
    c: Coincident(g10,g11)
    c: Coincident(g11,g12)
    c: Coincident(g12,g9)
    c: Horizontal(g9)
    c: Horizontal(g11)
    c: Vertical(g10)
    c: Vertical(g12)
    c: Diameter(g13) = 3
    c: Equal(g13,g14)
    c: Equal(g14,g15)
    c: Equal(g15,g16)
    c: DistanceX(g13,g14) = 23.75
    c: Horizontal(g14,g13)
    c: Vertical(g13,g16)
    c: Horizontal(g16,g15)
    c: Vertical(g14,g15)
    c: DistanceY(g16,g13) = 23.75
    c: DistanceX(g9,g14) = 2
    c: DistanceX(g13,g9) = 2
    c: DistanceY(g9,g13) = 2
    c: DistanceY(g16,g11) = 2
    c: Equal(g17,g18)
    c: Equal(g18,g20)
    c: Equal(g20,g19)
    c: Equal(g19,g16)
    c: Horizontal(g18,g17)
    c: Horizontal(g19,g20)
    c: Vertical(g17,g19)
    c: Vertical(g18,g20)
    c: DistanceY(g19,g17) = 23.75
    c: DistanceX(g17,g18) = 23.75
    c: Coincident(g21,g22)
    c: Coincident(g22,g23)
    c: Coincident(g23,g24)
    c: Coincident(g24,g21)
    c: Horizontal(g21)
    c: Horizontal(g23)
    c: Vertical(g22)
    c: Vertical(g24)
    c: DistanceX(g17,g21) = 2
    c: DistanceX(g21,g18) = 2
    c: DistanceY(g21,g17) = 2
    c: DistanceY(g19,g23) = 2
    c: Vertical(g16,g17)
    c: DistanceY(g14,g1) = 32
    c: DistanceY(g18,g15) = 48
    c: DistanceX(g20,g2) = 43
    c: Coincident(g25,g26)
    c: Coincident(g26,g27)
    c: Coincident(g27,g28)
    c: Coincident(g28,g25)
    c: Horizontal(g25)
    c: Horizontal(g27)
    c: Vertical(g26)
    c: Vertical(g28)
    c: Coincident(g29,g30)
    c: Coincident(g30,g31)
    c: Coincident(g31,g32)
    c: Coincident(g32,g29)
    c: Horizontal(g29)
    c: Horizontal(g31)
    c: Vertical(g30)
    c: Vertical(g32)
    c: DistanceY(g26,g26) = 8
    c: DistanceX(g25,g25) = 7
    c: DistanceY(g25,g13) = 3
    c: DistanceX(g25,g13) = 3
    c: DistanceX(g29,g29) = 7
    c: DistanceY(g30,g30) = 8
    c: DistanceY(g29,g17) = 3
    c: DistanceX(g29,g17) = 3
FEATURE [PartDesign::Pad] Pad019  label="PAD_ElectronicsBox_Cover"
  Direction = (0,0,1)
  Length = 3
  Length2 = 10
  Profile = -> Sketch046
  ReferenceAxis = -> Sketch046 [N_Axis]
  Type = 0
FEATURE [Sketcher::SketchObject] Sketch047  label="S_ElectronicsBox_NutInset"
  AttachmentOffset = pos=(0,0,-83) rot=(0,0,1;0rad)
  ExternalGeometry = -> [Sketch042]
  FullyConstrained = true
  MapMode = 5
  Placement = pos=(0,83,1.84e-14) rot=(1,0,0;1.5708rad)
  Support = -> [XZ_Plane027]
  sketch-geometry (6):
    g0: LineSegment StartX=-77.5 StartY=54.5 StartZ=0 EndX=-70.5 EndY=54.5 EndZ=0
    g1: LineSegment StartX=-70.5 StartY=54.5 StartZ=0 EndX=-70.5 EndY=51.5 EndZ=0
    g2: LineSegment StartX=-70.5 StartY=51.5 StartZ=0 EndX=-77.5 EndY=51.5 EndZ=0
    g3: LineSegment StartX=-77.5 StartY=51.5 StartZ=0 EndX=-77.5 EndY=54.5 EndZ=0
    g4: LineSegment StartX=-79 StartY=56 StartZ=0 EndX=-77.5 EndY=54.5 EndZ=0
    g5: LineSegment StartX=-69 StartY=56 StartZ=0 EndX=-70.5 EndY=54.5 EndZ=0
  constraints (16):
    c: Coincident(g0,g1)
    c: Coincident(g1,g2)
    c: Coincident(g2,g3)
    c: Coincident(g3,g0)
    c: Horizontal(g0)
    c: Horizontal(g2)
    c: Vertical(g1)
    c: Vertical(g3)
    c: DistanceX(g2,g1) = 7
    c: DistanceY(g1,g0) = 3
    c: Coincident(g4,g-4)
    c: Coincident(g4,g0)
    c: Coincident(g5,g-3)
    c: Coincident(g5,g0)
    c: Equal(g5,g4)
    c: DistanceY(g0,g4) = 1.5
FEATURE [PartDesign::Pocket] Pocket021  label="POCKET_ElectronicsBox_NutInset"
  BaseFeature = -> Pocket014
  Direction = (0,1,2e-16)
  Length = 10
  Length2 = 5
  Profile = -> Sketch047
  ReferenceAxis = -> Sketch047 [N_Axis]
  Reversed = true
  Type = 0
FEATURE [PartDesign::Mirrored] Mirrored  label="XFORM_ElectronicsBox_NutInsets_X"
  MirrorPlane = -> YZ_Plane027
FEATURE [PartDesign::Mirrored] Mirrored001  label="XFORM_ElectronicsBox_NutInsets_Y"
  MirrorPlane = -> XZ_Plane027
FEATURE [PartDesign::MultiTransform] MultiTransform  label="PAT_ElectronicsBox_NutInsets"
  BaseFeature = -> Pocket021
  Originals = -> [AdditiveLoft,Pocket021,Pocket014]
  Transformations = -> [Mirrored,Mirrored001]
FEATURE [PartDesign::Pad] Pad020  label="PAD_S_ElectronicsBox_HolePads"
  BaseFeature = -> MultiTransform
  Direction = (0,0,1)
  Length = 10
  Length2 = 10
  Profile = -> Sketch035
  ReferenceAxis = -> Sketch035 [N_Axis]
  Type = 0
FEATURE [PartDesign::Pocket] Pocket022  label="POCKET_ElectronicsBox_Holes"
  BaseFeature = -> Pad020
  Direction = (0,0,1)
  Length = 5
  Length2 = 5
  Profile = -> Sketch036
  ReferenceAxis = -> Sketch036 [N_Axis]
  Type = 1
FEATURE [PartDesign::Pocket] Pocket023  label="POCKET_ElectronicsBox_BoltIndent"
  BaseFeature = -> Pocket022
  Direction = (0,0,1)
  Length = 3
  Length2 = 5
  Profile = -> Sketch037
  ReferenceAxis = -> Sketch037 [N_Axis]
  Type = 0
FEATURE [PartDesign::Pocket] Pocket024  label="POCKET_ElectronicsBox_Switches"
  BaseFeature = -> Pocket023
  Direction = (0,1,-2e-16)
  Length = 5
  Length2 = 5
  Profile = -> Sketch038
  ReferenceAxis = -> Sketch038 [N_Axis]
  Type = 0
FEATURE [PartDesign::Pocket] Pocket025  label="POCKET_ElectronicsBox_BackWires"
  BaseFeature = -> Pocket024
  Direction = (0,-1,2e-16)
  Length = 5
  Length2 = 5
  Profile = -> Sketch045
  ReferenceAxis = -> Sketch045 [N_Axis]
  Type = 0
FEATURE [PartDesign::Body] B_ElectronicsBox  label="B_ElectronicsBox_Base"
  Group = -> [Sketch033,Pad016,Sketch034,Sketch035,Sketch036,Sketch037,Sketch038,Sketch039,Pad017,Sketch040,Sketch041,Sketch042,Sketch043,AdditiveLoft,Sketch045,Pocket014,Sketch047,Pocket021,MultiTransform,Mirrored,Mirrored001,Pad020,Pocket022,Pocket023,Pocket024,Pocket025]
  Origin = -> Origin027
  Tip = -> Pocket025
FEATURE [PartDesign::CoordinateSystem] LCS_ElectronicsBox_Fan0
  AttacherType = Attacher::AttachEngine3D
  Placement = pos=(29,37,3) rot=(0,0,1;0rad)
FEATURE [PartDesign::CoordinateSystem] LCA_ElectronicsBox_Fan1
  AttacherType = Attacher::AttachEngine3D
  Placement = pos=(29,-34,3) rot=(0,0,1;0rad)
FEATURE [PartDesign::CoordinateSystem] LCS_ElectronicsBox_Base_Arduino_Hole0
  AttacherType = Attacher::AttachEngine3D
  MapMode = 11
  Placement = pos=(-56,-39,11.5) rot=(0.707107,-0.707107,0;3.14159rad)
FEATURE [PartDesign::CoordinateSystem] LCS_ElectronicsBox_Base_Arduino_Hole1
  AttacherType = Attacher::AttachEngine3D
  MapMode = 11
  Placement = pos=(-56,36.5,11.5) rot=(0.707107,-0.707107,0;3.14159rad)
FEATURE [PartDesign::CoordinateSystem] LCS_ElectronicsBox_Base_Arduino_Hole2
  AttacherType = Attacher::AttachEngine3D
  MapMode = 11
  Placement = pos=(-8,-40.5,11.5) rot=(0.707107,-0.707107,0;3.14159rad)
FEATURE [PartDesign::CoordinateSystem] LCS_ElectronicsBox_Base_Arduino_Hole3
  AttacherType = Attacher::AttachEngine3D
  MapMode = 11
  Placement = pos=(-8,41.5,11.5) rot=(0.707107,-0.707107,0;3.14159rad)
FEATURE [PartDesign::CoordinateSystem] LCS_ElectronicsBox_Base_CNCShield0_Hole0
  AttacherType = Attacher::AttachEngine3D
  MapMode = 11
  Placement = pos=(19.25,-60,11.5) rot=(0.707107,-0.707107,0;3.14159rad)
FEATURE [PartDesign::CoordinateSystem] LCS_ElectronicsBox_Base_CNCShield0_Hole1
  AttacherType = Attacher::AttachEngine3D
  MapMode = 11
  Placement = pos=(19.25,-13,11.5) rot=(0.707107,-0.707107,0;3.14159rad)
FEATURE [PartDesign::CoordinateSystem] LCS_ElectronicsBox_Base_CNCShield1_Hole1
  AttacherType = Attacher::AttachEngine3D
  MapMode = 11
  Placement = pos=(19.25,60,11.5) rot=(0.707107,-0.707107,0;3.14159rad)
FEATURE [PartDesign::CoordinateSystem] LCS_ElectronicsBox_Base_CNCShield1_Hole0
  AttacherType = Attacher::AttachEngine3D
  MapMode = 11
  Placement = pos=(19.25,13,11.5) rot=(0.707107,-0.707107,0;3.14159rad)
FEATURE [PartDesign::CoordinateSystem] LCS_ElectronicsBox_Base_TopHole0
  AttacherType = Attacher::AttachEngine3D
  MapMode = 11
  Placement = pos=(-74,-77,56) rot=(0,0,1;1.5708rad)
FEATURE [PartDesign::CoordinateSystem] LCS_ElectronicsBox_Base_TopHole1
  AttacherType = Attacher::AttachEngine3D
  MapMode = 11
  Placement = pos=(-74,77,56) rot=(0,0,1;1.5708rad)
FEATURE [PartDesign::CoordinateSystem] LCS_ElectronicsBox_Base_TopHole002  label="LCS_ElectronicsBox_Base_TopHole2"
  AttacherType = Attacher::AttachEngine3D
  MapMode = 11
  Placement = pos=(74,-77,56) rot=(0,0,-1;1.5708rad)
FEATURE [PartDesign::CoordinateSystem] LCS_ElectronicsBox_Base_TopHole3
  AttacherType = Attacher::AttachEngine3D
  MapMode = 11
  Placement = pos=(74,77,56) rot=(0,0,-1;1.5708rad)
FEATURE [PartDesign::CoordinateSystem] LCS_ElectronicsBox_Base_Mount0
  AttacherType = Attacher::AttachEngine3D
  MapMode = 11
  Placement = pos=(-90,-58,2) rot=(0,0,1;1.5708rad)
FEATURE [PartDesign::CoordinateSystem] LCS_ElectronicsBox_Base_Mount1
  AttacherType = Attacher::AttachEngine3D
  MapMode = 11
  Placement = pos=(-90,58,2) rot=(0,0,1;1.5708rad)
FEATURE [PartDesign::CoordinateSystem] LCS_ElectronicsBox_Base_Mount2
  AttacherType = Attacher::AttachEngine3D
  MapMode = 11
  Placement = pos=(90,-58,2) rot=(0,0,1;1.5708rad)
FEATURE [PartDesign::CoordinateSystem] LCS_ElectronicsBox_Base_Mount3
  AttacherType = Attacher::AttachEngine3D
  MapMode = 11
  Placement = pos=(90,58,2) rot=(0,0,1;1.5708rad)
FEATURE [PartDesign::CoordinateSystem] LCS_ElectronicsBox_Base_Switch
  AttacherType = Attacher::AttachEngine3D
  Placement = pos=(7.41,-73,35.5) rot=(0,0,1;0rad)
  expr: .Placement.Base.x = <<S_ElectronicsBox_Switches>>.Constraints.SwitchX
  expr: .Placement.Base.z = <<S_ElectronicsBox_Switches>>.Constraints.SwitchY
FEATURE [PartDesign::CoordinateSystem] LCS_ElectronicsBox_Base_USB
  AttacherType = Attacher::AttachEngine3D
  Placement = pos=(-44,-73,23.5) rot=(0,0,1;0rad)
  expr: .Placement.Base.x = -<<S_ElectronicsBox_Switches>>.Constraints.USBX
  expr: .Placement.Base.z = <<S_ElectronicsBox_Switches>>.Constraints.USBY
FEATURE [PartDesign::CoordinateSystem] LCS_ElectronicsBox_Base_PowerCable
  AttacherType = Attacher::AttachEngine3D
  Placement = pos=(-44,73,20) rot=(0,0,1;0rad)
  expr: .Placement.Base.x = -<<S_ElectronicsBox_BackWires>>.Constraints.PowerX
  expr: .Placement.Base.z = <<S_ElectronicsBox_BackWires>>.Constraints.PowerY
FEATURE [App::Part] P_ElectronicsBox  label="P_ElectronicsBox_Base"
  DrawingName = jrobot-electronics-parts.FCStd
  Group = -> [B_ElectronicsBox,LCS_ElectronicsBox_Lid,LCS_Origin006,LCS_ElectronicsBox_Base_Arduino_Hole0,LCS_ElectronicsBox_Base_Arduino_Hole1,LCS_ElectronicsBox_Base_Arduino_Hole2,LCS_ElectronicsBox_Base_Arduino_Hole3,LCS_ElectronicsBox_Base_CNCShield0_Hole0,LCS_ElectronicsBox_Base_CNCShield0_Hole1,LCS_ElectronicsBox_Base_CNCShield1_Hole1,LCS_ElectronicsBox_Base_CNCShield1_Hole0,+11 more]
  Origin = -> Origin026
  PartDescription = B_ElectronicsBox_Base
  PartID = jrobot-electronics-parts
FEATURE [Sketcher::SketchObject] Sketch  label="S_ElectronixBox_Cover_Walls"
  ExternalGeometry = -> [Sketch046]
  FullyConstrained = true
  MapMode = 5
  Support = -> [XY_Plane029]
  sketch-geometry (8):
    g0: LineSegment StartX=85 StartY=-69.8 StartZ=0 EndX=82 EndY=-69.8 EndZ=0
    g1: LineSegment StartX=82 StartY=-69.8 StartZ=0 EndX=82 EndY=69.8 EndZ=0
    g2: LineSegment StartX=82 StartY=69.8 StartZ=0 EndX=85 EndY=69.8 EndZ=0
    g3: LineSegment StartX=85 StartY=69.8 StartZ=0 EndX=85 EndY=-69.8 EndZ=0
    g4: LineSegment StartX=-85 StartY=-69.8 StartZ=0 EndX=-82 EndY=-69.8 EndZ=0
    g5: LineSegment StartX=-82 StartY=-69.8 StartZ=0 EndX=-82 EndY=69.8 EndZ=0
    g6: LineSegment StartX=-82 StartY=69.8 StartZ=0 EndX=-85 EndY=69.8 EndZ=0
    g7: LineSegment StartX=-85 StartY=69.8 StartZ=0 EndX=-85 EndY=-69.8 EndZ=0
  constraints (24):
    c: Coincident(g0,g1)
    c: Coincident(g1,g2)
    c: Coincident(g2,g3)
    c: Coincident(g3,g0)
    c: Horizontal(g0)
    c: Horizontal(g2)
    c: Vertical(g1)
    c: Vertical(g3)
    c: Coincident(g4,g5)
    c: Coincident(g5,g6)
    c: Coincident(g6,g7)
    c: Coincident(g7,g4)
    c: Horizontal(g4)
    c: Horizontal(g6)
    c: Vertical(g5)
    c: Vertical(g7)
    c: Horizontal(g5,g1)
    c: Equal(g4,g0)
    c: Horizontal(g4,g0)
    c: DistanceX(g4,g4) = 3
    c: Vertical(g4,g-3)
    c: Vertical(g0,g-4)
    c: DistanceY(g2,g-6) = 11.2
    c: DistanceY(g-4,g0) = 11.2
FEATURE [PartDesign::Pad] Pad  label="PAD_ElectronixBox_Cover_Walls"
  BaseFeature = -> Pad019
  Direction = (0,0,1)
  Length = 53.6
  Length2 = 10
  Profile = -> Sketch
  ReferenceAxis = -> Sketch [N_Axis]
  Reversed = true
  Type = 0
FEATURE [Sketcher::SketchObject] Sketch048
  AttachmentOffset = pos=(-50,-50,85) rot=(0,0,1;0rad)
  FullyConstrained = true
  MapMode = 5
  Placement = pos=(85,-50,-50) rot=(0.57735,0.57735,0.57735;2.0944rad)
  Support = -> [YZ_Plane029]
  sketch-geometry (4):
    g0: ArcOfCircle CenterX=-10 CenterY=0 CenterZ=0 NormalX=0 NormalY=0 NormalZ=1 AngleXU=0 Radius=1 StartAngle=1.5708 EndAngle=4.71239
    g1: ArcOfCircle CenterX=10 CenterY=0 CenterZ=0 NormalX=0 NormalY=0 NormalZ=1 AngleXU=0 Radius=1 StartAngle=4.71239 EndAngle=7.85398
    g2: LineSegment StartX=-10 StartY=-1 StartZ=0 EndX=10 EndY=-1 EndZ=0
    g3: LineSegment StartX=10 StartY=1 StartZ=0 EndX=-10 EndY=1 EndZ=0
  constraints (9):
    c: Tangent(g0,g2) = -1.5708
    c: Tangent(g2,g1) = -1.5708
    c: Tangent(g1,g3) = -1.5708
    c: Tangent(g3,g0) = -1.5708
    c: Equal(g0,g1)
    c: PointOnObject(g0,g-1)
    c: DistanceY(g0,g0) = 2
    c: Symmetric(g0,g1,g-1)
    c: DistanceX(g0,g1) = 20
FEATURE [PartDesign::Pocket] Pocket
  BaseFeature = -> Pad
  Direction = (-1,2e-16,-3e-16)
  Length = 5
  Length2 = 5
  Profile = -> Sketch048
  ReferenceAxis = -> Sketch048 [N_Axis]
  Type = 0
FEATURE [PartDesign::LinearPattern] LinearPattern
  Direction = -> Sketch048 [H_Axis]
  Length = 100
  Occurrences = 5
FEATURE [PartDesign::LinearPattern] LinearPattern001
  Direction = -> Sketch048 [V_Axis]
  Length = 45
  Occurrences = 8
FEATURE [PartDesign::Mirrored] Mirrored002
  MirrorPlane = -> YZ_Plane029
FEATURE [PartDesign::MultiTransform] MultiTransform001
  BaseFeature = -> Pocket
  Originals = -> [Pocket]
  Transformations = -> [LinearPattern,LinearPattern001,Mirrored002]
FEATURE [PartDesign::Body] Body011  label="B_ElectronicsBox_Cover"
  Group = -> [Sketch046,Pad019,Sketch,Pad,Sketch048,Pocket,MultiTransform001,LinearPattern,LinearPattern001,Mirrored002]
  Origin = -> Origin029
  Tip = -> MultiTransform001
FEATURE [App::Part] P_ElectronicsBox_Cover
  DrawingName = jrobot-electronics-parts.FCStd
  Group = -> [LCS_Origin007,Body011,LCS_ElectronicsBox_Fan0,LCA_ElectronicsBox_Fan1]
  Origin = -> Origin028
  PartDescription = B_ElectronicsBox_Cover
  PartID = jrobot-electronics-parts
FEATURE [App::DocumentObjectGroup] Group011  label="ElectronicsEnclosure"
  Group = -> [P_ElectronicsBox,P_ElectronicsBox_Cover]
FEATURE [App::DocumentObjectGroup] Group007  label="Robot"
  Group = -> [Group011]
FEATURE [App::DocumentObjectGroup] Group  label="Parts"
  Group = -> [Group007]
